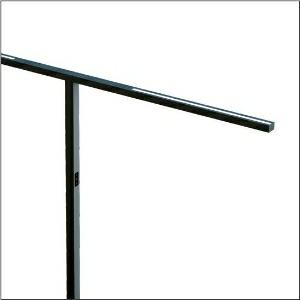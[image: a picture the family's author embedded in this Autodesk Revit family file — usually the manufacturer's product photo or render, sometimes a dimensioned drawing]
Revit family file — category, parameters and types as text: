
# Revit family: silica_r__31_floor_duo_51my52hmtcb_73f4
name_source: partatom
category: Lighting Fixtures
units: mm (PartAtom-declared; Revit-internal decimal feet)

## family parameters
Cut with Voids When Loaded = No
Host = Face
Light Source = No
Part Type = Normal
Room Calculation Point = No
Round Connector Dimension = Use Diameter
Shared = No

## types (1)
- --- (1 x LED, 17040 lm, 142 W, 4000K)
    Apparent Load = 142 VA
    CIE Flux Codes = 86 100 100 24 100
    Color Rendering = 80
    Color Temperature = 4000K
    Default Elevation = 1800 mm
    Description = Silica® 31 Floor duo, floorstanding luminaire, secondary optical cover: cover panel, of PMMA, light emission: direct/indirect distribution, primary light characteristic: symmetric, installation type: not mounted, LED, rated luminous flux: 17.040lm, luminous efficacy: 120lm/W, light colour: 8tw, colour temperature: 2700..6500K, control gear: Touchdim, daylight-dependent control, with cable with plug, mains connection: 230V, AC, 50Hz, rated input power: 142W, luminaire head, of aluminium, coated, jet black (RAL 9005), length: 2.372mm, width: 52mm, supporting column, angular, of aluminium, coated, jet black (RAL 9005), baseplate, of steel, coated, jet black (RAL 9005), protection rating (complete): IP20, insulation class (complete): insulation class I (protective earthing), certification: CE, permissible operating ambient temperature: -20..+40°C, standard: EN 50419, packaging unit: 1 piece
    Height = 36 mm
    Lamp = 1 x LED
    Lamp Light Flux = 17040 lm
    Lamp Power = 142 W
    Lamp count = 1
    Length = 2372 mm
    Luminous efficacy = 120 lm/W
    Manufacturer = Siteco
    ModVariant = No
    Model = 51MY52HMTCB
    Mounting Place = Floor
    Mounting Type = Freestanding
    Number of Poles = 1
    OnlyDefault = Yes
    Power Factor = 1
    Product Name = Silica® 31 Floor duo
    Product group = floorstanding luminaire
    ProductGroupID = 1302
    Protection Class = Protection class I
    Protection Degree = IP 20
    RLX_Detail_Level = 1
    RLX_Emergency_Light_Flux = 0 lm
    RLX_Emergency_Type = 0
    RLX_Emergency_Type_DB = No
    RlxData = <blob elided: 21601 chars, md5=e01965ab>
    Socket = socket
    Standby Power = 0 W
    System Light Flux = 17040 lm
    System Power = 142 W
    Type Comments = factory setting
    Type Image = l_1275315.jpg
    URL = http://relux.com
    VarID = @adj_080218
    Voltage = 0 V
    Weight = 0.00 kg
    Width = 52 mm  [stored 0.170604 ft]

note: [stored X ft] marks values corroborated as IEEE doubles in the binary element streams (Revit-internal decimal feet)

## geometry (parser evidence)
native form markers: Blend x4, Sweep x13
no freeform markers — native parametric forms only
